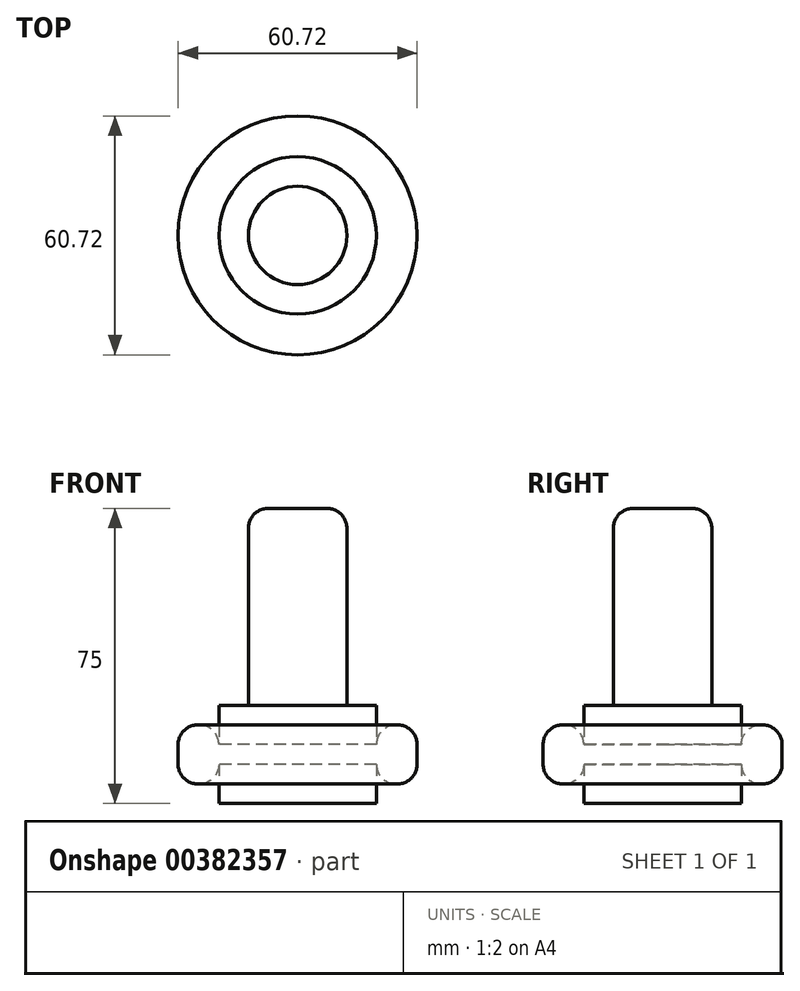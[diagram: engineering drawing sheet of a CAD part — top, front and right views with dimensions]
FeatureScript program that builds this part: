
annotation { "Feature Type Name" : "Feature", "Feature Type Description" : "" }
export const myFeature = defineFeature(function(context is Context, id is Id, definition is map)
    precondition{}
    {
        {
            var Q0;
            Q0=qCreatedBy(makeId("Top.planeOp"),FACE);
            var sketch = newSketch(context, id + "F0", { "sketchPlane" : qUnion([Q0])});
            skCircle(sketch, "E0", {"center": v(0, 0) * mm, "radius": 30.36 * mm});
            skCircle(sketch, "E1", {"center": v(0, 0) * mm, "radius": 20 * mm});
            skSolve(sketch);
        }
        {
            var Q0;
            Q0=makeQuery(id+"F0.imprint","IMPRINT",FACE,{"disambiguationData":[TD([[makeQuery(id+"F0.imprint","IMPRINT",EDGE,{"derivedFrom":sQuery(id+"F0.wireOp",EDGE,"E0")}),1.0]])]});
            extrude(context, id + "F1", {"entities" : qUnion([Q0]), "endBound" : BoundingType.SYMMETRIC, "depth" : 15 * mm});
        }
        {
            var Q0;
            Q0=makeQuery(id+"F1.opExtrude","CAP_EDGE",EDGE,{"disambiguationData":[OSD([sQuery(id+"F0.wireOp",EDGE,"E0")])],"isStart":true});
            var Q1;
            Q1=makeQuery(id+"F1.opExtrude","CAP_EDGE",EDGE,{"disambiguationData":[OSD([sQuery(id+"F0.wireOp",EDGE,"E1")])],"isStart":true});
            fillet(context, id + "F2", {"entities" : qUnion([Q0, Q1]), "radius" : 5 * mm, "tangentPropagation" : true, "allowEdgeOverflow" : false});
        }
        {
            var Q0;
            Q0=makeQuery(id+"F1.opExtrude","CAP_EDGE",EDGE,{"disambiguationData":[OSD([sQuery(id+"F0.wireOp",EDGE,"E1")])],"isStart":false});
            fillet(context, id + "F3", {"entities" : qUnion([Q0]), "radius" : 5 * mm, "tangentPropagation" : true, "allowEdgeOverflow" : false});
        }
        {
            var Q0;
            Q0=makeQuery(id+"F1.opExtrude","CAP_EDGE",EDGE,{"disambiguationData":[OSD([sQuery(id+"F0.wireOp",EDGE,"E0")])],"isStart":false});
            fillet(context, id + "F4", {"entities" : qUnion([Q0]), "radius" : 5 * mm, "tangentPropagation" : true, "allowEdgeOverflow" : false});
        }
        {
            var Q0;
            Q0=makeQuery(id+"F0.imprint","IMPRINT",FACE,{"disambiguationData":[TD([[makeQuery(id+"F0.imprint","IMPRINT",EDGE,{"derivedFrom":sQuery(id+"F0.wireOp",EDGE,"E1")}),1.0]])]});
            extrude(context, id + "F5", {"entities" : qUnion([Q0]), "operationType" : NewBodyOperationType.ADD, "endBound" : BoundingType.SYMMETRIC, "depth" : 25 * mm});
        }
        {
            var Q0;
            Q0=makeQuery(id+"F5.opExtrude","CAP_FACE",FACE,{"disambiguationData":[OSD([sQuery(id+"F0.wireOp",EDGE,"E1")])],"isStart":false});
            var sketch = newSketch(context, id + "F6", { "sketchPlane" : qUnion([Q0])});
            skCircle(sketch, "E2", {"center": v(0, 0) * mm, "radius": 12.5 * mm});
            skSolve(sketch);
        }
        {
            var Q0;
            Q0=makeQuery(id+"F6.imprint","IMPRINT",FACE,{"disambiguationData":[TD([[makeQuery(id+"F6.imprint","IMPRINT",EDGE,{"derivedFrom":sQuery(id+"F6.wireOp",EDGE,"E2")}),1.0]])]});
            extrude(context, id + "F7", {"entities" : qUnion([Q0]), "operationType" : NewBodyOperationType.ADD, "depth" : 50 * mm});
        }
        {
            var Q0;
            Q0=makeQuery(id+"F7.opExtrude","CAP_FACE",FACE,{"disambiguationData":[OSD([sQuery(id+"F6.wireOp",EDGE,"E2")])],"isStart":false});
            fillet(context, id + "F8", {"entities" : qUnion([Q0]), "radius" : 5 * mm, "tangentPropagation" : true, "allowEdgeOverflow" : false});
        }
    });
